# Revit family: Soap_Dispenser-Surface_Mounted-Bobrick-ClassicSeries-B-42
name_source: partatom
category: Specialty Equipment
revit_build: Autodesk Revit 2014 (Build: 20130308_1515(x64)
units: mm (PartAtom-declared; Revit-internal decimal feet)

## types (1)
- B-42
    Assembly Code = C1030200
    Capacity = 40-fl oz (1.2-L)
    Default Elevation = 50"
    Description = Soap Dispenser For Liquid And Lotion Soaps, And Detergents
    Finish = ABS Plastic (Black)
    Height = 6 7/8"
    Length = 3 3/8"
    Manufacturer = Bobrick Washroom Equipment, Inc.
    Material = ABS Plastic (Black)
    Model = B-42
    Product Documentation Link = http://products.bobrick.com
    Product Page URL = http://products.bobrick.com
    Specification = Soap dispenser shall have black, high-impact-resistant ABS wall bracket, lid, push button, and spout. Bracket shall be equipped with a locking device to secure lid, container, and a removable plastic key to disengage locking device. Vandal-resistant lid shall pivot up for top filling only after lock is disengaged. Corrosion-resistant valve shall have soap head-holding mushroom valve, stainless steel spring, U-packing seal, and duckbill; and shall dispense commercially marketed all-purpose hand soaps. Valve shall be operable with one hand and with less than 5 pounds of force (22.2 N) to comply with accessible design (including ADAAG in U.S.A.). Container shall be black, translucent ABS with a capacity of 40-fl oz (1.2-L), be retained to the wall bracket by a sliding latch and a container stop spring tab and shall be removable for maintenance or replacement.
    URL = http://www.bobrick.com
    Width = 5 13/16"

## geometry (parser evidence)
native form markers: Blend x2, Sweep x2
no freeform markers — native parametric forms only
